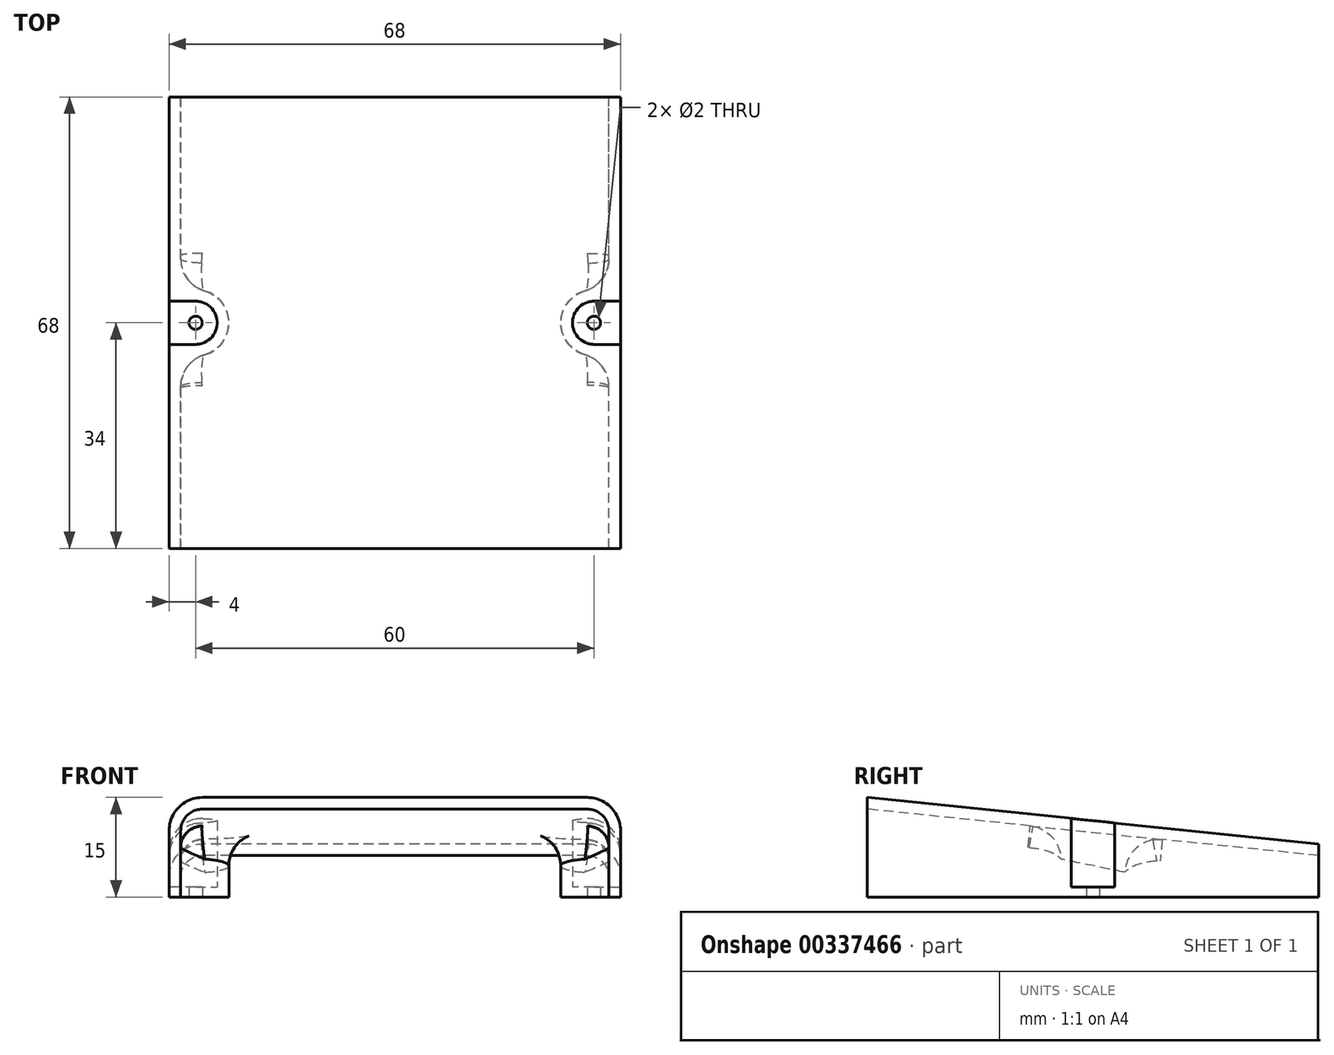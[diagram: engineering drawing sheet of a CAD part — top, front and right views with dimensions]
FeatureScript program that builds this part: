
annotation { "Feature Type Name" : "Feature", "Feature Type Description" : "" }
export const myFeature = defineFeature(function(context is Context, id is Id, definition is map)
    precondition{}
    {
        {
            var Q0;
            Q0=qCreatedBy(makeId("Right.planeOp"),FACE);
            var sketch = newSketch(context, id + "F0", { "sketchPlane" : qUnion([Q0])});
            skLineSegment(sketch, "E0.bottom", {"start": v(-34, 0) * mm, "end": v(34, 0) * mm});
            skLineSegment(sketch, "E1", {"start": v(-34, 0) * mm, "end": v(-34, 15) * mm});
            skLineSegment(sketch, "E2", {"start": v(-34, 15) * mm, "end": v(34, 8) * mm});
            skLineSegment(sketch, "E3", {"start": v(34, 8) * mm, "end": v(34, 0) * mm});
            skLineSegment(sketch, "E4", {"start": v(0, -56.66) * mm, "end": v(0, 58.83) * mm, "construction": true});
            skSolve(sketch);
        }
        {
            var Q0;
            Q0 = qSketchRegion(id + "F0", true);
            extrude(context, id + "F1", {"entities" : qUnion([Q0]), "depth" : 68 / 2 * mm, "hasSecondDirection" : true, "secondDirectionOppositeDirection" : true, "secondDirectionDepth" : 68 / 2 * mm});
        }
        {
            var Q0;
            Q0=makeQuery(id+"F1.opExtrude","CAP_EDGE",EDGE,{"disambiguationData":[OSD([sQuery(id+"F0.wireOp",EDGE,"E2")])],"isStart":false});
            var Q1;
            Q1=makeQuery(id+"F1.opExtrude","CAP_EDGE",EDGE,{"disambiguationData":[OSD([sQuery(id+"F0.wireOp",EDGE,"E2")])],"isStart":true});
            fillet(context, id + "F2", {"entities" : qUnion([Q0, Q1]), "radius" : 5 * mm, "tangentPropagation" : true, "allowEdgeOverflow" : false});
        }
        {
            var Q0;
            Q0=qCreatedBy(makeId("Top.planeOp"),FACE);
            var sketch = newSketch(context, id + "F3", { "sketchPlane" : qUnion([Q0])});
            skCircle(sketch, "E5", {"center": v(-30, 0) * mm, "radius": 1 * mm});
            skCircle(sketch, "E6", {"center": v(30, 0) * mm, "radius": 1 * mm});
            skLineSegment(sketch, "E7", {"start": v(0, -59.31) * mm, "end": v(0, 47.59) * mm, "construction": true});
            skSolve(sketch);
        }
        {
            var Q0;
            Q0 = qSketchRegion(id + "F3", true);
            extrude(context, id + "F4", {"entities" : qUnion([Q0]), "operationType" : NewBodyOperationType.REMOVE, "depth" : 39 * mm});
        }
        {
            var Q0;
            Q0=qCreatedBy(makeId("Top.planeOp"),FACE);
            cPlane(context, id + "F5", {"entities" : qUnion([Q0]), "cplaneType" : CPlaneType.OFFSET, "offset" : 1.5 * mm, "width" : 150 * mm, "height" : 150 * mm});
        }
        {
            var Q0;
            Q0=qCreatedBy(id+"F5.planeOp",FACE);
            var sketch = newSketch(context, id + "F6", { "sketchPlane" : qUnion([Q0])});
            skArc(sketch, "E8", {"start": v(-30, -3.25) * mm, "mid": v(-26.75, 0) * mm, "end": v(-30, 3.25) * mm});
            skLineSegment(sketch, "E9.bottom", {"start": v(-30, 3.25) * mm, "end": v(-36.72, 3.25) * mm});
            skLineSegment(sketch, "E9.top", {"start": v(-30, -3.25) * mm, "end": v(-36.72, -3.25) * mm});
            skLineSegment(sketch, "E9.right", {"start": v(-36.72, 3.25) * mm, "end": v(-36.72, -3.25) * mm});
            skLineSegment(sketch, "E10", {"start": v(0, -51.5) * mm, "end": v(0, 51.02) * mm, "construction": true});
            skLineSegment(sketch, "E11.MirrorCS", {"start": v(30, 3.25) * mm, "end": v(36.72, 3.25) * mm});
            skArc(sketch, "E12.MirrorCS", {"start": v(30, -3.25) * mm, "mid": v(26.75, 0) * mm, "end": v(30, 3.25) * mm});
            skLineSegment(sketch, "E13.MirrorCS", {"start": v(30, -3.25) * mm, "end": v(36.72, -3.25) * mm});
            skLineSegment(sketch, "E14.MirrorCS", {"start": v(36.72, 3.25) * mm, "end": v(36.72, -3.25) * mm});
            skSolve(sketch);
        }
        {
            var Q0;
            Q0 = qSketchRegion(id + "F6", true);
            extrude(context, id + "F7", {"entities" : qUnion([Q0]), "operationType" : NewBodyOperationType.REMOVE, "depth" : 25 * mm});
        }
        {
            var Q0;
            Q0=makeQuery(id+"F1.opExtrude","SWEPT_FACE",FACE,{"disambiguationData":[OSD([sQuery(id+"F0.wireOp",EDGE,"E0.bottom")])]});
            var Q1;
            Q1=makeQuery(id+"F1.opExtrude","SWEPT_FACE",FACE,{"disambiguationData":[OSD([sQuery(id+"F0.wireOp",EDGE,"E1")])]});
            var Q2;
            Q2=makeQuery(id+"F1.opExtrude","SWEPT_FACE",FACE,{"disambiguationData":[OSD([sQuery(id+"F0.wireOp",EDGE,"E3")])]});
            shell(context, id + "F8", {"entities" : qUnion([Q0, Q1, Q2]), "thickness" : 1.75 * mm});
        }
        {
            var Q0;
            Q0=makeQuery(id+"F8.opShell","OFFSET_EDGE",EDGE,{"disambiguationData":[OSD([sQuery(id+"F0.wireOp",EDGE,"E0.bottom"),sQuery(id+"F0.wireOp",EDGE,"E1"),sQuery(id+"F0.wireOp",EDGE,"E2"),sQuery(id+"F0.wireOp",EDGE,"E3"),sQuery(id+"F6.wireOp",EDGE,"E13.MirrorCS")])]});
            var Q1;
            Q1=makeQuery(id+"F8.opShell","OFFSET_EDGE",EDGE,{"disambiguationData":[OSD([sQuery(id+"F0.wireOp",EDGE,"E0.bottom"),sQuery(id+"F0.wireOp",EDGE,"E1"),sQuery(id+"F0.wireOp",EDGE,"E2"),sQuery(id+"F0.wireOp",EDGE,"E3"),sQuery(id+"F6.wireOp",EDGE,"E9.top")])]});
            fillet(context, id + "F9", {"entities" : qUnion([Q0, Q1]), "radius" : 5 * mm, "tangentPropagation" : true, "allowEdgeOverflow" : false});
        }
    });
